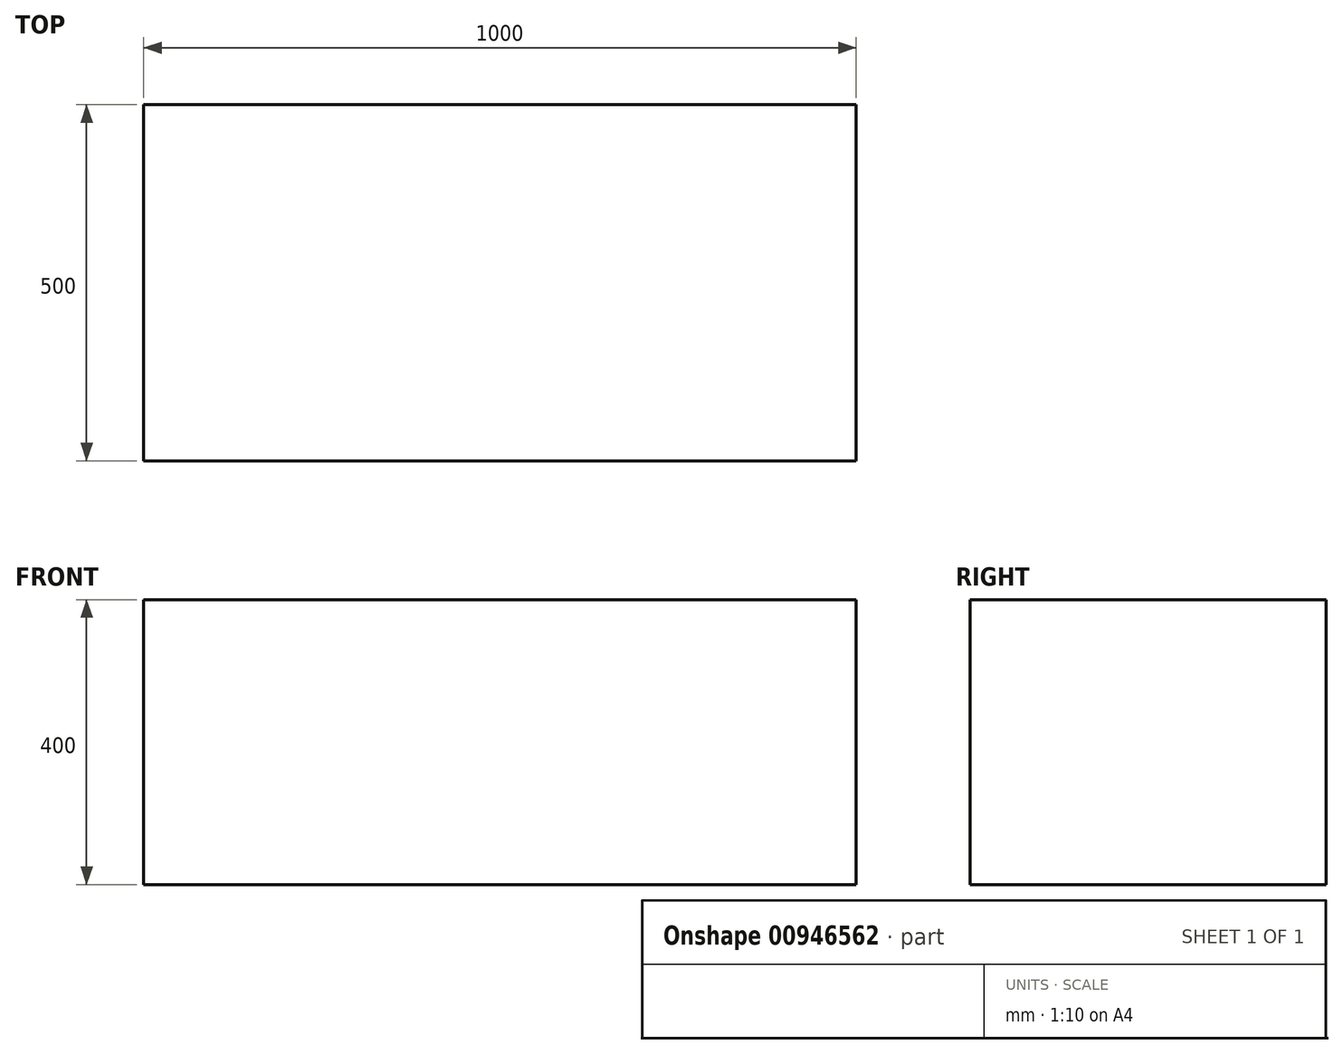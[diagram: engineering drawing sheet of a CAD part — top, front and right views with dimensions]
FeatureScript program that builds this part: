
annotation { "Feature Type Name" : "Feature", "Feature Type Description" : "" }
export const myFeature = defineFeature(function(context is Context, id is Id, definition is map)
    precondition{}
    {
        {
            var Q0;
            Q0=qCreatedBy(makeId("Top.planeOp"),FACE);
            var sketch = newSketch(context, id + "F0", { "sketchPlane" : qUnion([Q0])});
            skLineSegment(sketch, "E0.bottom", {"start": v(500, -250) * mm, "end": v(-500, -250) * mm});
            skLineSegment(sketch, "E0.top", {"start": v(500, 250) * mm, "end": v(-500, 250) * mm});
            skLineSegment(sketch, "E0.left", {"start": v(500, -250) * mm, "end": v(500, 250) * mm});
            skLineSegment(sketch, "E0.right", {"start": v(-500, -250) * mm, "end": v(-500, 250) * mm});
            skPoint(sketch, "E0.middle", {"position": v(0, 0) * mm});
            skSolve(sketch);
        }
        {
            var Q0;
            Q0 = qSketchRegion(id + "F0", true);
            extrude(context, id + "F1", {"entities" : qUnion([Q0]), "depth" : 400 * mm, "offsetDistance" : 25 * mm});
        }
    });
